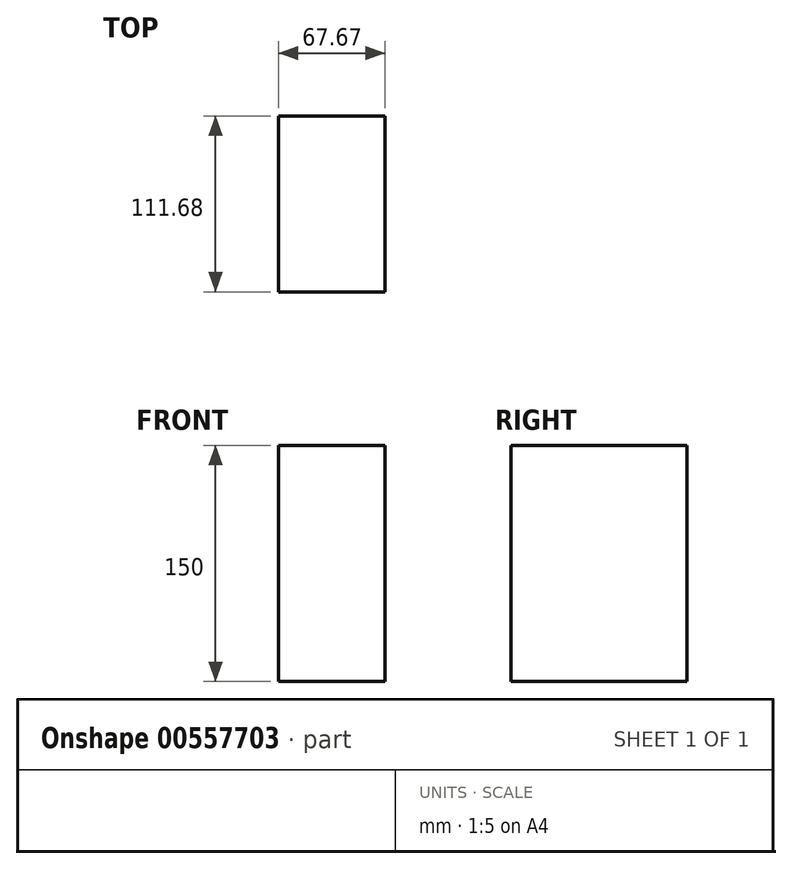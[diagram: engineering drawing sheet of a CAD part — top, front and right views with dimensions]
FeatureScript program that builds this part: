
annotation { "Feature Type Name" : "Feature", "Feature Type Description" : "" }
export const myFeature = defineFeature(function(context is Context, id is Id, definition is map)
    precondition{}
    {
        {
            var Q0;
            Q0=qCreatedBy(makeId("Top.planeOp"),FACE);
            var sketch = newSketch(context, id + "F0", { "sketchPlane" : qUnion([Q0])});
            skLineSegment(sketch, "E0.bottom", {"start": v(-45.28, -43.12) * mm, "end": v(22.39, -43.12) * mm});
            skLineSegment(sketch, "E0.top", {"start": v(-45.28, 68.56) * mm, "end": v(22.39, 68.56) * mm});
            skLineSegment(sketch, "E0.left", {"start": v(-45.28, -43.12) * mm, "end": v(-45.28, 68.56) * mm});
            skLineSegment(sketch, "E0.right", {"start": v(22.39, -43.12) * mm, "end": v(22.39, 68.56) * mm});
            skSolve(sketch);
        }
        {
            var Q0;
            Q0=makeQuery(id+"F0.imprint","IMPRINT",FACE,{"disambiguationData":[TD([[makeQuery(id+"F0.imprint","IMPRINT",EDGE,{"derivedFrom":sQuery(id+"F0.wireOp",EDGE,"E0.bottom")}),1.0]])]});
            extrude(context, id + "F1", {"entities" : qUnion([Q0]), "depth" : 150 * mm, "offsetDistance" : 25.4 * mm});
        }
    });
